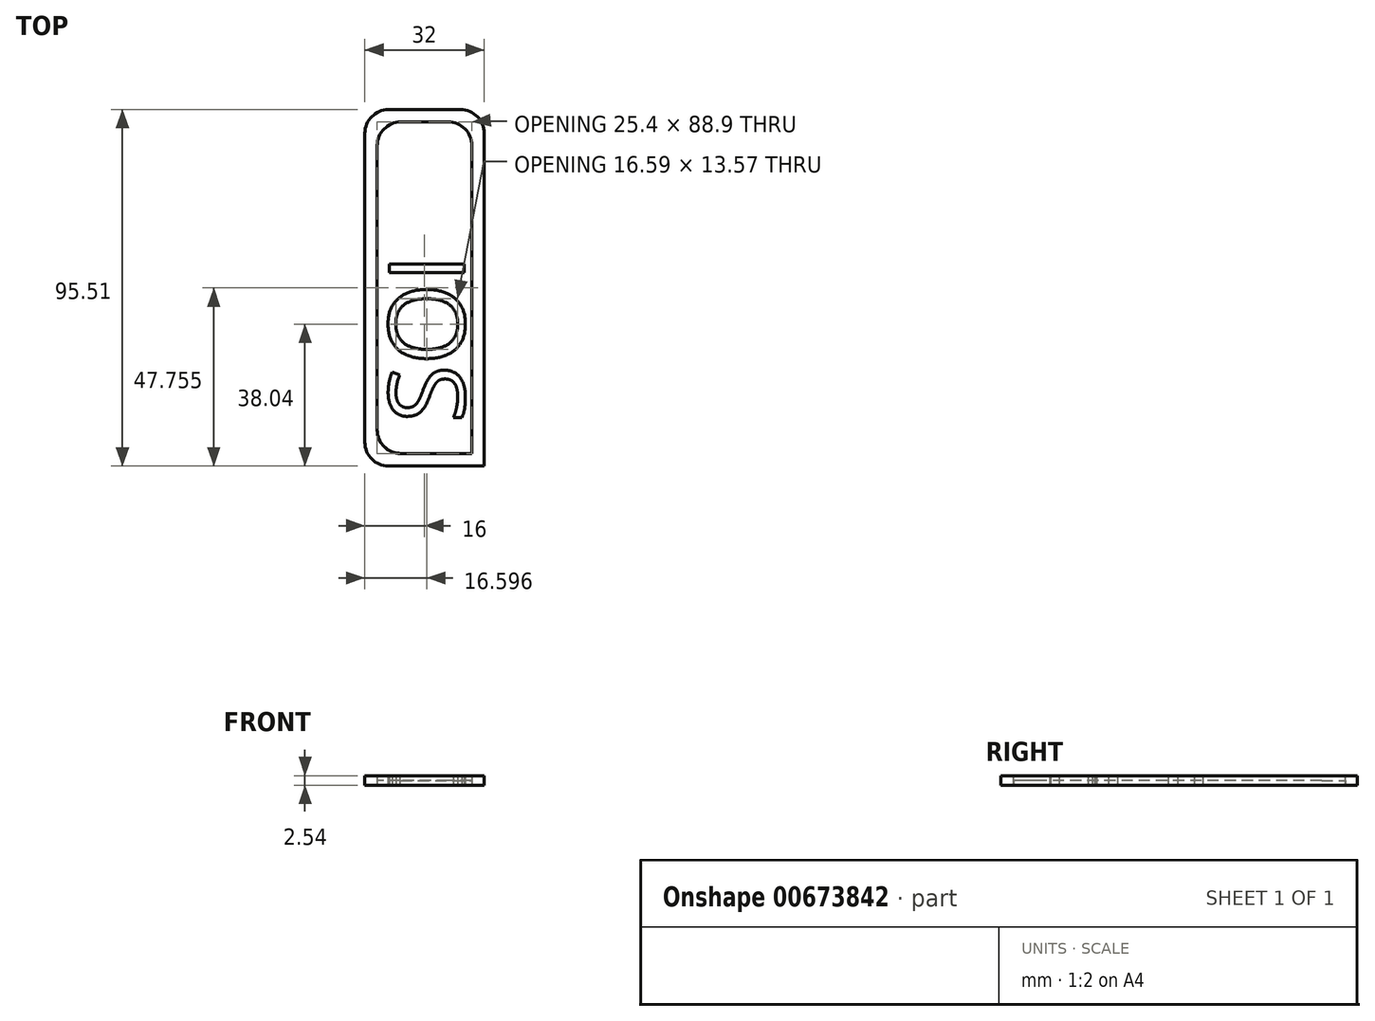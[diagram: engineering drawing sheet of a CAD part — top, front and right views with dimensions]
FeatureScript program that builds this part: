
annotation { "Feature Type Name" : "Feature", "Feature Type Description" : "" }
export const myFeature = defineFeature(function(context is Context, id is Id, definition is map)
    precondition{}
    {
        {
            var Q0;
            Q0=qCreatedBy(makeId("Top.planeOp"),FACE);
            var sketch = newSketch(context, id + "F0", { "sketchPlane" : qUnion([Q0])});
            skLineSegment(sketch, "E0.bottom", {"start": v(-6.35, 40.2) * mm, "end": v(0, 40.2) * mm});
            skLineSegment(sketch, "E0.top", {"start": v(-6.35, -48.7) * mm, "end": v(0, -48.7) * mm});
            skLineSegment(sketch, "E0.left", {"start": v(-12.7, 33.84) * mm, "end": v(-12.7, -42.36) * mm});
            skLineSegment(sketch, "E1.MirrorCS", {"start": v(6.35, 40.2) * mm, "end": v(0, 40.2) * mm});
            skLineSegment(sketch, "E2.MirrorCS", {"start": v(12.7, 33.84) * mm, "end": v(12.7, -48.7) * mm});
            skLineSegment(sketch, "E3.MirrorCS", {"start": v(12.7, -48.7) * mm, "end": v(0, -48.7) * mm});
            skLineSegment(sketch, "E4.0", {"start": v(-16, 37.15) * mm, "end": v(-16, -45.66) * mm});
            skLineSegment(sketch, "E4.1", {"start": v(9.65, 43.5) * mm, "end": v(0, 43.5) * mm});
            skLineSegment(sketch, "E4.2", {"start": v(16, 37.15) * mm, "end": v(16, -52) * mm});
            skLineSegment(sketch, "E4.3", {"start": v(-9.65, 43.5) * mm, "end": v(0, 43.5) * mm});
            skLineSegment(sketch, "E4.4", {"start": v(16, -52) * mm, "end": v(0, -52) * mm});
            skLineSegment(sketch, "E4.5", {"start": v(-9.65, -52) * mm, "end": v(0, -52) * mm});
            skPoint(sketch, "E5.visualSharp", {"position": v(-16, 43.5) * mm});
            skArc(sketch, "E5.filletArc", {"start": v(-9.65, 43.5) * mm, "mid": v(-14.14, 41.64) * mm, "end": v(-16, 37.15) * mm});
            skPoint(sketch, "E6.visualSharp", {"position": v(-12.7, 40.2) * mm});
            skArc(sketch, "E6.filletArc", {"start": v(-6.35, 40.2) * mm, "mid": v(-10.84, 38.33) * mm, "end": v(-12.7, 33.84) * mm});
            skPoint(sketch, "E7.visualSharp", {"position": v(16, 43.5) * mm});
            skArc(sketch, "E7.filletArc", {"start": v(16, 37.15) * mm, "mid": v(14.14, 41.64) * mm, "end": v(9.65, 43.5) * mm});
            skPoint(sketch, "E8.visualSharp", {"position": v(12.7, 40.2) * mm});
            skArc(sketch, "E8.filletArc", {"start": v(12.7, 33.84) * mm, "mid": v(10.84, 38.33) * mm, "end": v(6.35, 40.2) * mm});
            skPoint(sketch, "E9.visualSharp", {"position": v(-16, -52) * mm});
            skArc(sketch, "E9.filletArc", {"start": v(-16, -45.66) * mm, "mid": v(-14.14, -50.15) * mm, "end": v(-9.65, -52) * mm});
            skPoint(sketch, "E10.visualSharp", {"position": v(16, -52) * mm});
            skLineSegment(sketch, "E10.filletArc", {"start": v(16, -52) * mm, "end": v(16, -52) * mm});
            skPoint(sketch, "E11.visualSharp", {"position": v(-12.7, -48.7) * mm});
            skArc(sketch, "E11.filletArc", {"start": v(-12.7, -42.36) * mm, "mid": v(-10.84, -46.85) * mm, "end": v(-6.35, -48.7) * mm});
            skPoint(sketch, "E12.visualSharp", {"position": v(12.7, -48.7) * mm});
            skLineSegment(sketch, "E12.filletArc", {"start": v(12.7, -48.7) * mm, "end": v(12.7, -48.7) * mm});
            skText(sketch, "E13", { "text": "SOI", "fontName": "OpenSans-Regular.ttf"});
            const initialGuessF0  = {"E13": [0.01067, -0.04045, 0, 1, 0.02032]};
            skSetInitialGuess(sketch, initialGuessF0);
            skSolve(sketch);
        }
        {
            var Q0;
            Q0=makeQuery(id+"F0.imprint","IMPRINT",FACE,{"disambiguationData":[TD([[makeQuery(id+"F0.imprint","IMPRINT",EDGE,{"derivedFrom":sQuery(id+"F0.wireOp",EDGE,"E13.sketch_text.stroke-41")}),-1.0]])]});
            var Q1;
            Q1=makeQuery(id+"F0.imprint","IMPRINT",FACE,{"disambiguationData":[TD([[makeQuery(id+"F0.imprint","IMPRINT",EDGE,{"derivedFrom":sQuery(id+"F0.wireOp",EDGE,"E13.sketch_text.stroke-0")}),-1.0]])]});
            var Q2;
            Q2=makeQuery(id+"F0.imprint","IMPRINT",FACE,{"disambiguationData":[TD([[makeQuery(id+"F0.imprint","IMPRINT",EDGE,{"derivedFrom":sQuery(id+"F0.wireOp",EDGE,"E13.sketch_text.stroke-25")}),-1.0]])]});
            var Q3;
            Q3=makeQuery(id+"F0.imprint","IMPRINT",FACE,{"disambiguationData":[TD([[makeQuery(id+"F0.imprint","IMPRINT",EDGE,{"derivedFrom":sQuery(id+"F0.wireOp",EDGE,"E0.bottom")}),1.0]])]});
            extrude(context, id + "F1", {"entities" : qUnion([Q0, Q1, Q2, Q3]), "depth" : 2.54 * mm, "offsetDistance" : 25.4 * mm});
        }
        {
            var Q0;
            Q0=qCreatedBy(makeId("Top.planeOp"),FACE);
            var sketch = newSketch(context, id + "F2", { "sketchPlane" : qUnion([Q0])});
            skLineSegment(sketch, "E14.bottom", {"start": v(-6.37, 40.27) * mm, "end": v(-0.02, 40.27) * mm});
            skLineSegment(sketch, "E14.top", {"start": v(-6.37, -48.63) * mm, "end": v(-0.02, -48.63) * mm});
            skLineSegment(sketch, "E14.left", {"start": v(-12.72, 33.92) * mm, "end": v(-12.72, -42.28) * mm});
            skLineSegment(sketch, "E15.MirrorCS", {"start": v(6.33, 40.27) * mm, "end": v(-0.02, 40.27) * mm});
            skLineSegment(sketch, "E16.MirrorCS", {"start": v(12.68, 33.92) * mm, "end": v(12.68, -48.63) * mm});
            skLineSegment(sketch, "E17.MirrorCS", {"start": v(12.68, -48.63) * mm, "end": v(-0.02, -48.63) * mm});
            skArc(sketch, "E18.filletArc", {"start": v(-6.37, 40.27) * mm, "mid": v(-10.86, 38.41) * mm, "end": v(-12.72, 33.92) * mm});
            skArc(sketch, "E19.filletArc", {"start": v(12.68, 33.92) * mm, "mid": v(10.82, 38.41) * mm, "end": v(6.33, 40.27) * mm});
            skArc(sketch, "E20.filletArc", {"start": v(-12.72, -42.28) * mm, "mid": v(-10.86, -46.77) * mm, "end": v(-6.37, -48.63) * mm});
            skSolve(sketch);
        }
        {
            var Q0;
            Q0 = qSketchRegion(id + "F2", true);
            extrude(context, id + "F3", {"entities" : qUnion([Q0]), "depth" : 1.27 * mm, "offsetDistance" : 25.4 * mm});
        }
    });
